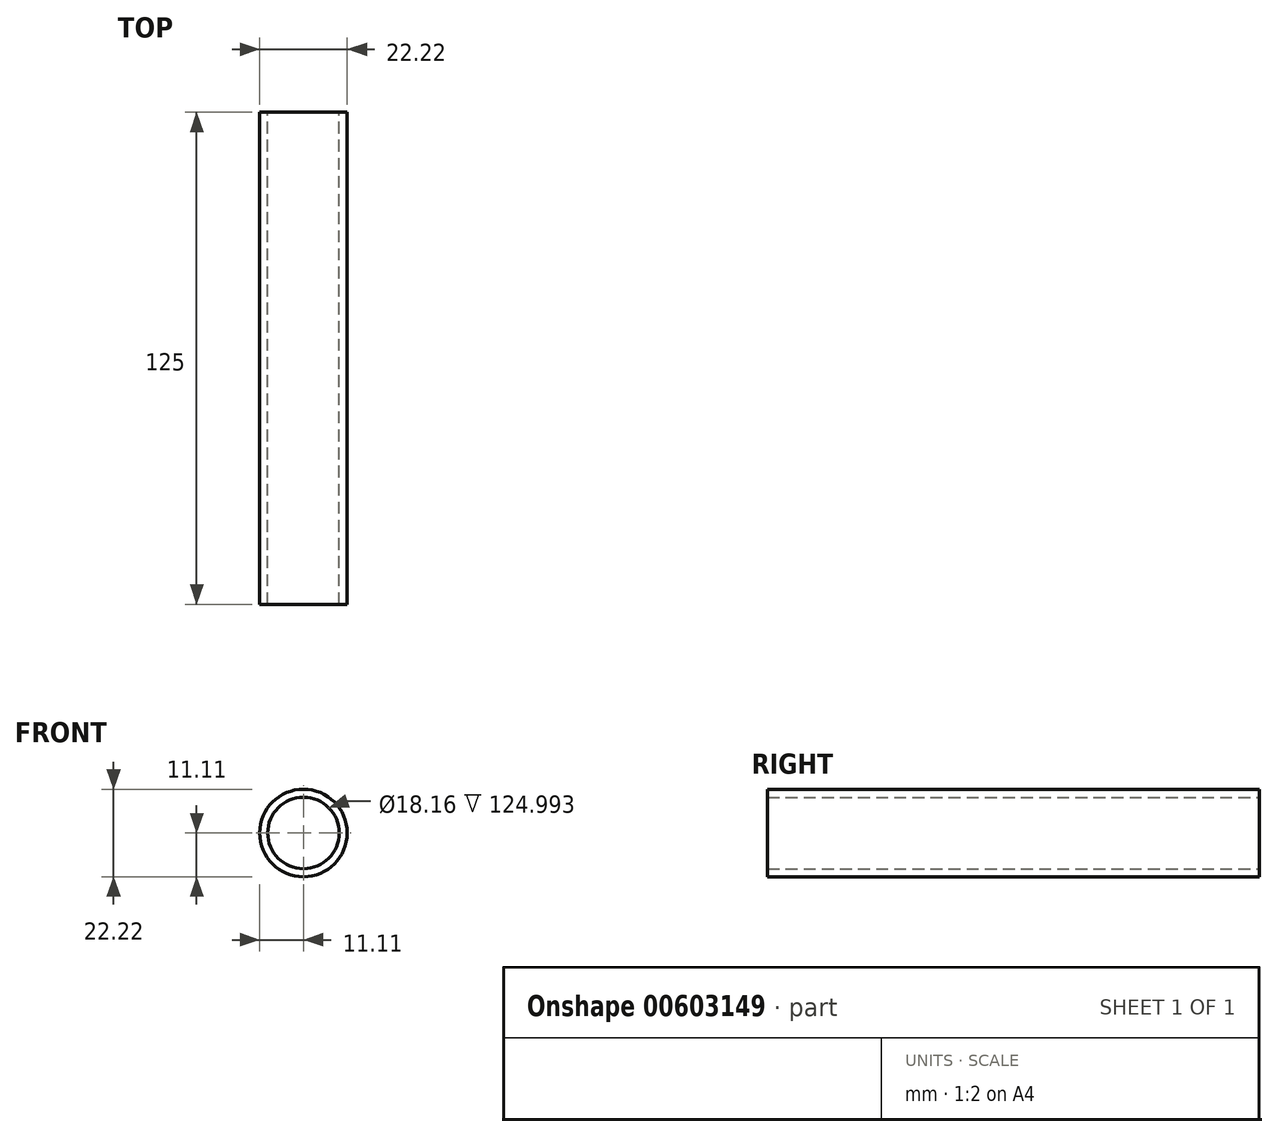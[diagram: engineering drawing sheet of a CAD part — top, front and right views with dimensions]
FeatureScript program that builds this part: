
annotation { "Feature Type Name" : "Feature", "Feature Type Description" : "" }
export const myFeature = defineFeature(function(context is Context, id is Id, definition is map)
    precondition{}
    {
        {
            var Q0;
            Q0=qCreatedBy(makeId("Front.planeOp"),FACE);
            var sketch = newSketch(context, id + "F0", { "sketchPlane" : qUnion([Q0])});
            skCircle(sketch, "E0", {"center": v(0, 0) * mm, "radius": 9.08 * mm});
            skCircle(sketch, "E1", {"center": v(0, 0) * mm, "radius": 11.11 * mm});
            skSolve(sketch);
        }
        {
            var Q0;
            Q0=makeQuery(id+"F0.imprint","IMPRINT",FACE,{"disambiguationData":[TD([[makeQuery(id+"F0.imprint","IMPRINT",EDGE,{"derivedFrom":sQuery(id+"F0.wireOp",EDGE,"E0")}),-1.0]])]});
            extrude(context, id + "F1", {"entities" : qUnion([Q0]), "endBound" : BoundingType.SYMMETRIC, "depth" : 125 * mm, "offsetDistance" : 25.4 * mm});
        }
    });
